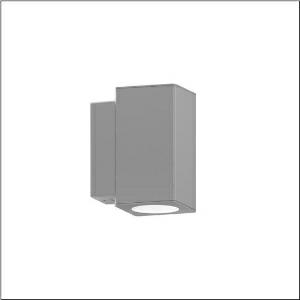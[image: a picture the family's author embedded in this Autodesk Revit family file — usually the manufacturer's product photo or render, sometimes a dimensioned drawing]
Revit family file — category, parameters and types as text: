
# Revit family: cl_31_wand_5cl563623
name_source: partatom
category: Lighting Fixtures
units: mm (PartAtom-declared; Revit-internal decimal feet)

## family parameters
Cut with Voids When Loaded = No
Host = Face
Light Source = No
Part Type = Normal
Room Calculation Point = No
Round Connector Dimension = Use Diameter
Shared = No

## types (1)
- --- (1 x LED, 600 lm, 5.4 W, 3000K)
    Apparent Load = 5 VA
    CIE Flux Codes = 98 100 100 50 100
    Color Rendering = 80
    Color Temperature = 3000K
    Default Elevation = 1800 mm
    Description = CL 31 Wall, wall luminaire, primary light control with reflector, of aluminium, primary optical cover: cover panel, of glass, transparent, light emission: up/down distribution, primary light characteristic: symmetric, installation type: surface-mounted, for 2x LED, rated luminous flux: 300lm, luminous efficacy: 110lm/W, light colour: 830, colour temperature: 3000K, control gear: DALI, with terminal, 5-pole, max. 2.5mm², mains connection: 220..240V, AC, 50/60Hz, rated input power: 5.5W, luminaire housing, square, of aluminium, powder-coated, SITECO metallic grey, length: 143mm, width: 100mm, height: 186mm, protection rating (complete): IP65, insulation class (complete): insulation class I (protective earthing), certification: CE, ENEC, impact resistance: IK08, permissible operating ambient temperature for outdoor applications: -20..+50°C, packaging unit: 1 piece
    Height = 186 mm
    Lamp = 1 x LED
    Lamp Light Flux = 600 lm
    Lamp Power = 5.4 W
    Lamp count = 1
    Length = 100 mm  [stored 0.328084 ft]
    Luminous efficacy = 111 lm/W
    Manufacturer = Siteco
    ModVariant = No
    Model = 5CL563623
    Mounting Place = Wall
    Mounting Type = Surface mounted
    Number of Poles = 1
    OnlyDefault = Yes
    Power Factor = 1
    Product Name = CL 31 Wand
    Product group = wall luminaire
    ProductGroupID = 2003
    Protection Class = Protection class I
    Protection Degree = IP 65
    RLX_Detail_Level = 1
    RLX_Emergency_Light_Flux = 0 lm
    RLX_Emergency_Type = 0
    RLX_Emergency_Type_DB = No
    RlxData = <blob elided: 40469 chars, md5=fb1332b9>
    Socket = socket
    Standby Power = 0 W
    System Light Flux = 600 lm
    System Power = 5 W
    Type Comments = factory setting: luminous flux: 100 % | dim-lin: 254 | 135 mA
    Type Image = l_1006895.jpg
    URL = http://relux.com
    VarID = @adj_192887
    Voltage = 0 V
    Weight = 0.00 kg
    Width = 143 mm

note: [stored X ft] marks values corroborated as IEEE doubles in the binary element streams (Revit-internal decimal feet)

## geometry (parser evidence)
native form markers: Blend x4, Sweep x10
no freeform markers — native parametric forms only
